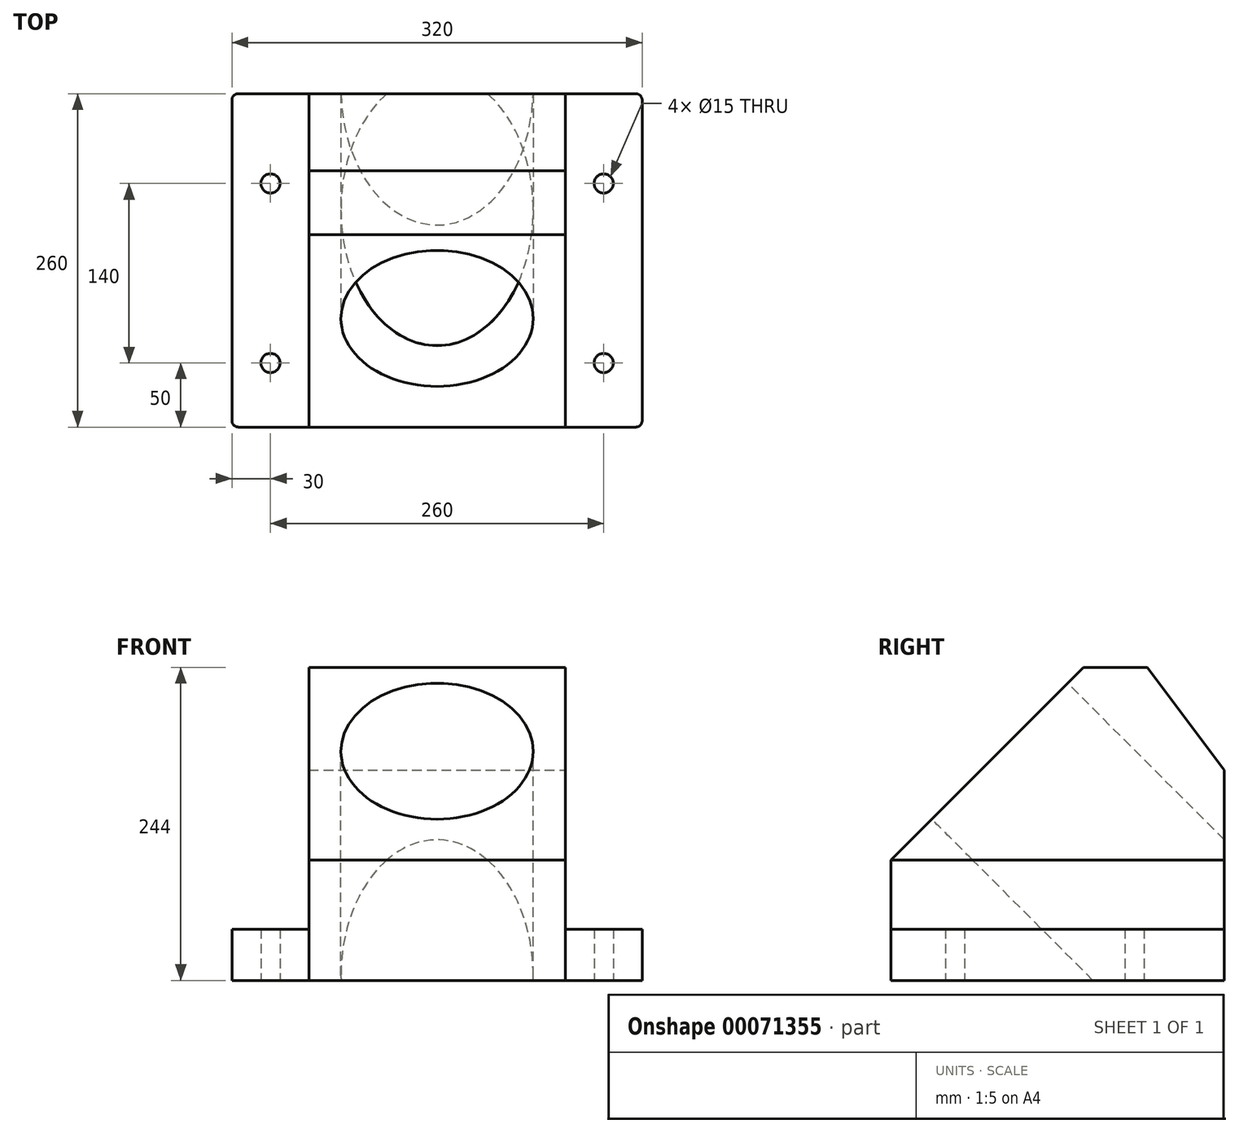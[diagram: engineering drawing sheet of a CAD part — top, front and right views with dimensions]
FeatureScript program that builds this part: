
annotation { "Feature Type Name" : "Feature", "Feature Type Description" : "" }
export const myFeature = defineFeature(function(context is Context, id is Id, definition is map)
    precondition{}
    {
        {
            var Q0;
            Q0=qCreatedBy(makeId("Top.planeOp"),FACE);
            var sketch = newSketch(context, id + "F0", { "sketchPlane" : qUnion([Q0])});
            skLineSegment(sketch, "E0.bottom", {"start": v(160, -130) * mm, "end": v(-160, -130) * mm});
            skLineSegment(sketch, "E0.top", {"start": v(160, 130) * mm, "end": v(-160, 130) * mm});
            skLineSegment(sketch, "E0.left", {"start": v(160, -130) * mm, "end": v(160, 130) * mm});
            skLineSegment(sketch, "E0.right", {"start": v(-160, -130) * mm, "end": v(-160, 130) * mm});
            skPoint(sketch, "E0.middle", {"position": v(0, 0) * mm});
            skCircle(sketch, "E1", {"center": v(-130, 60) * mm, "radius": 7.5 * mm});
            skCircle(sketch, "E2", {"center": v(-130, -80) * mm, "radius": 7.5 * mm});
            skLineSegment(sketch, "E3", {"start": v(-100, 130) * mm, "end": v(-100, -130) * mm});
            skLineSegment(sketch, "E4", {"start": v(0, 130) * mm, "end": v(0, -130) * mm, "construction": true});
            skLineSegment(sketch, "E5.MirrorCS", {"start": v(100, 130) * mm, "end": v(100, -130) * mm});
            skCircle(sketch, "E6.MirrorC", {"center": v(130, 60) * mm, "radius": 7.5 * mm});
            skCircle(sketch, "E7.MirrorC", {"center": v(130, -80) * mm, "radius": 7.5 * mm});
            skSolve(sketch);
        }
        {
            var Q0;
            {var subQ1=sQuery(id+"F0.wireOp",EDGE,"E0.left");Q0=makeQuery(id+"F0.imprint","IMPRINT",FACE,{"disambiguationData":[TD([[makeQuery(id+"F0.imprint","IMPRINT",EDGE,{"derivedFrom":subQ1}),1.0]])]});}
            var Q1;
            {var subQ0=sQuery(id+"F0.wireOp",EDGE,"E0.right");Q1=makeQuery(id+"F0.imprint","IMPRINT",FACE,{"disambiguationData":[TD([[makeQuery(id+"F0.imprint","IMPRINT",EDGE,{"derivedFrom":subQ0}),-1.0]])]});}
            extrude(context, id + "F1", {"entities" : qUnion([Q0, Q1]), "depth" : 40 * mm});
        }
        {
            var Q0;
            {var subQ0=sQuery(id+"F0.wireOp",EDGE,"E3");Q0=makeQuery(id+"F0.imprint","IMPRINT",FACE,{"disambiguationData":[TD([[makeQuery(id+"F0.imprint","IMPRINT",EDGE,{"derivedFrom":subQ0}),1.0]])]});}
            extrude(context, id + "F2", {"entities" : qUnion([Q0]), "depth" : 94 * mm});
        }
        {
            var Q0;
            Q0=makeQuery(id+"F2.opExtrude","SWEPT_FACE",FACE,{"disambiguationData":[OSD([sQuery(id+"F0.wireOp",EDGE,"E5.MirrorCS")])]});
            var sketch = newSketch(context, id + "F3", { "sketchPlane" : qUnion([Q0])});
            skLineSegment(sketch, "E8", {"start": v(-130, 94) * mm, "end": v(20, 244) * mm});
            skLineSegment(sketch, "E9", {"start": v(20, 244) * mm, "end": v(70, 244) * mm});
            skLineSegment(sketch, "E10", {"start": v(70, 244) * mm, "end": v(130, 164) * mm});
            skLineSegment(sketch, "E11", {"start": v(130, 164) * mm, "end": v(130, 94) * mm});
            skSolve(sketch);
        }
        {
            var Q0;
            Q0=makeQuery(id+"F3.imprint","IMPRINT",FACE,{"disambiguationData":[TD([[makeQuery(id+"F3.imprint","IMPRINT",EDGE,{"derivedFrom":sQuery(id+"F3.wireOp",EDGE,"E8")}),-1.0]])]});
            extrude(context, id + "F4", {"entities" : qUnion([Q0]), "oppositeDirection" : true, "depth" : 200 * mm});
        }
        {
            var Q0;
            Q0=makeQuery(id+"F4.opExtrude","SWEPT_FACE",FACE,{"disambiguationData":[OSD([sQuery(id+"F3.wireOp",EDGE,"E8")])]});
            var sketch = newSketch(context, id + "F5", { "sketchPlane" : qUnion([Q0])});
            skCircle(sketch, "E12", {"center": v(0, 94.44) * mm, "radius": 75 * mm});
            skSolve(sketch);
        }
        {
            var Q0;
            Q0 = qSketchRegion(id + "F5", true);
            extrude(context, id + "F6", {"entities" : qUnion([Q0]), "operationType" : NewBodyOperationType.REMOVE, "oppositeDirection" : true, "depth" : 324.75 * mm});
        }
        {
            var Q0;
            Q0=makeQuery(id+"F1.opExtrude","SWEPT_EDGE",EDGE,{"disambiguationData":[OSD([sQuery(id+"F0.wireOp",EDGE,"E0.bottom"),sQuery(id+"F0.wireOp",EDGE,"E0.right")])]});
            var Q1;
            Q1=makeQuery(id+"F1.opExtrude","SWEPT_EDGE",EDGE,{"disambiguationData":[OSD([sQuery(id+"F0.wireOp",EDGE,"E0.bottom"),sQuery(id+"F0.wireOp",EDGE,"E0.left")])]});
            var Q2;
            Q2=makeQuery(id+"F1.opExtrude","SWEPT_EDGE",EDGE,{"disambiguationData":[OSD([sQuery(id+"F0.wireOp",EDGE,"E0.top"),sQuery(id+"F0.wireOp",EDGE,"E0.left")])]});
            var Q3;
            Q3=makeQuery(id+"F1.opExtrude","SWEPT_EDGE",EDGE,{"disambiguationData":[OSD([sQuery(id+"F0.wireOp",EDGE,"E0.top"),sQuery(id+"F0.wireOp",EDGE,"E0.right")])]});
            fillet(context, id + "F7", {"entities" : qUnion([Q0, Q1, Q2, Q3]), "radius" : 5 * mm, "tangentPropagation" : true, "allowEdgeOverflow" : false});
        }
    });
